# Revit family: HeartFelt-Linear-Luxalon Carrier Splice_HunterDouglasEurope.LOG200
name_source: partatom
category: Specialty Equipment
revit_build: Autodesk Revit 2016 (Build: 20150220_1215(x64)
units: mm (PartAtom-declared; Revit-internal decimal feet)

## family parameters
Always vertical = Yes
Cut with Voids When Loaded = No
OmniClass Number = 23.35.70.24.11.11.11
OmniClass Title = Suspended Ceilings, Suspension Assembly
Part Type = Normal
Room Calculation Point = No
Round Connector Dimension = Use Diameter
Shared = No
Work Plane-Based = No

## types (2) — shared parameters
Alloy = EN AW 5050
Article Code = 33.4173
EN13501-1_Fire rating = Class A2,s1,d0
Length = 177 mm
Manufacturer = Hunter Douglas
Model = Luxalon Carrier Splice
Product Data = http://assets2.hunterdouglascontract.com
Subcategory = HeartFelt® Ceilings
Thickness = 0.95 mm
URL = http://www.hunterdouglasarchitectural.eu

## per-type parameters (varying)
| type | Colour Code | Material |
| Luxalon Carrier Splice_Transparent Coated | 7178 | Aluminum-7178_HunterDouglasEurope |
| Luxalon Carrier Splice_Black | 1863 | Aluminum-1863_HunterDouglasEurope |

## geometry (parser evidence)
native form markers: Sweep x2
no freeform markers — native parametric forms only
